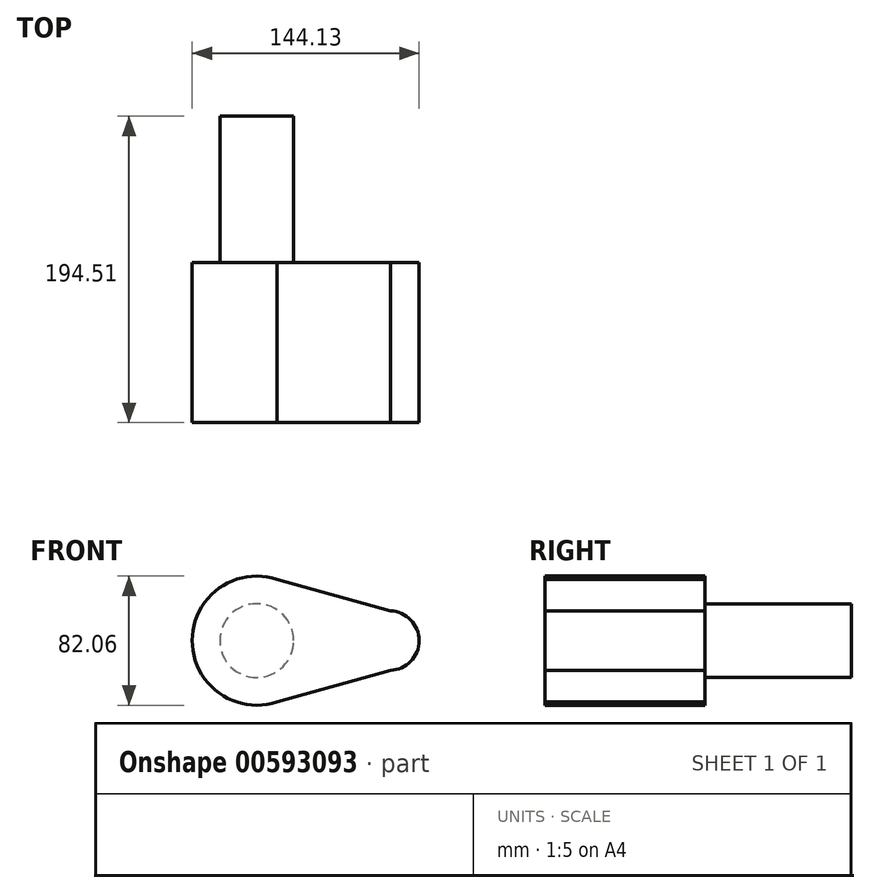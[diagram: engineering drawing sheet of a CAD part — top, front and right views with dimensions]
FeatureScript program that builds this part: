
annotation { "Feature Type Name" : "Feature", "Feature Type Description" : "" }
export const myFeature = defineFeature(function(context is Context, id is Id, definition is map)
    precondition{}
    {
        {
            var Q0;
            Q0=qCreatedBy(makeId("Front.planeOp"),FACE);
            var sketch = newSketch(context, id + "F0", { "sketchPlane" : qUnion([Q0])});
            skCircle(sketch, "E0", {"center": v(0, 0) * mm, "radius": 41.03 * mm});
            skCircle(sketch, "E1", {"center": v(84.15, 0) * mm, "radius": 18.95 * mm});
            skLineSegment(sketch, "E2", {"start": v(84.89, 18.93) * mm, "end": v(9.04, 40.02) * mm});
            skLineSegment(sketch, "E3", {"start": v(9.04, -40.02) * mm, "end": v(84.89, -18.93) * mm});
            skSolve(sketch);
        }
        {
            var Q0;
            Q0 = qSketchRegion(id + "F0", true);
            extrude(context, id + "F1", {"entities" : qUnion([Q0]), "endBound" : BoundingType.SYMMETRIC, "depth" : 101.6 * mm, "offsetDistance" : 25.4 * mm});
        }
        {
            var Q0;
            Q0=makeQuery(id+"F1.opExtrude","CAP_FACE",FACE,{"disambiguationData":[OSD([sQuery(id+"F0.wireOp",EDGE,"E0"),sQuery(id+"F0.wireOp",EDGE,"E1"),sQuery(id+"F0.wireOp",EDGE,"E2"),sQuery(id+"F0.wireOp",EDGE,"E3")])],"isStart":false});
            var sketch = newSketch(context, id + "F2", { "sketchPlane" : qUnion([Q0])});
            skCircle(sketch, "E4", {"center": v(0, 0) * mm, "radius": 23.4 * mm});
            skSolve(sketch);
        }
        {
            var Q0;
            Q0 = qSketchRegion(id + "F2", true);
            extrude(context, id + "F3", {"entities" : qUnion([Q0]), "operationType" : NewBodyOperationType.ADD, "endBound" : BoundingType.THROUGH_ALL, "oppositeDirection" : true, "depth" : 37.6 * mm, "offsetDistance" : 25.4 * mm});
        }
    });
